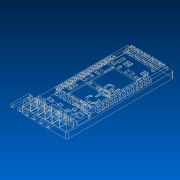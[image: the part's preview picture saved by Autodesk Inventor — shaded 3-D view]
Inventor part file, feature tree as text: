
AUTODESK INVENTOR PART (.ipt)
format: ipt  version: 2015 (Build 190159000, 159)  size: 1,295,360 bytes
history: native  units: mm
features: extrude x16, sketch x13, projected_geometry x8, fillet x5, pattern_linear x3, mirror x1, other x1
ambient origin geometry x8: Origin, YZ Plane, XZ Plane, XY Plane, X Axis, Y Axis, Z Axis, Center Point
bodies: Solid1 (feature_tree)
feature tree (47):
  extrude  "Extrusion1"  Depth=37.5mm
  sketch  "Sketch2"  dims[d2=2.0mm d3=0.0mm d9=0.0mm]
  sketch  "Sketch3"  dims[d12=1.0mm d13=0.0mm d14=1.2mm d15=0.0mm]
  extrude  "Extrusion2"  TaperAngle=0.0deg  [1 undecoded]
  extrude  "Extrusion3"  Depth=1.2mm TaperAngle=0.0deg
  extrude  "Extrusion4"  Depth=1.5mm TaperAngle=0.0deg
  extrude  "Extrusion5"  Depth=1.2mm TaperAngle=0.0deg
  extrude  "Extrusion6"  Depth=130.0mm
  extrude  "Extrusion7"  Depth=1.2mm TaperAngle=0.0deg
  fillet  "Fillet2"  Radius=0.5mm
  pattern_linear  "Rectangular Pattern1"  Count1=8 Spacing1=1.52mm
  mirror  "Mirror1"
  extrude  "Extrusion8"  Depth=0.8mm
  extrude  "Extrusion9"  Depth=4.0mm
  fillet  "Fillet4"  Radius=4.0mm
  pattern_linear  "Rectangular Pattern2"  Count1=6 Spacing1=2.51mm
  extrude  "Extrusion10"  Depth=0.8mm
  pattern_linear  "Rectangular Pattern3"  Spacing1=0.8mm  [1 undecoded]
  extrude  "Extrusion11"  Depth=0.2mm
  extrude  "Extrusion12"  Depth=0.2mm
  fillet  "Fillet5"  Radius=0.8mm
  fillet  "Fillet6"  Radius=0.8mm
  extrude  "Extrusion13"  Depth=2.0mm TaperAngle=0.0deg
  fillet  "Fillet7"  Radius=1.0mm
  extrude  "Extrusion14"  Depth=0.4mm
  extrude  "Extrusion15"  Depth=1.1mm TaperAngle=0.0deg
  extrude  "Extrusion16"  Depth=0.4mm
  sketch  "Sketch1"  dims[d0=16.1mm d1=37.5mm]
  other  "Image2"
  sketch  "Sketch4"  dims[d16=1.5mm d17=0.0mm d18=1.5mm d19=0.0mm]
  sketch  "Sketch5"  dims[d20=1.2mm d21=0.0mm d22=1.2mm d23=0.0mm]
  sketch  "Sketch7"  dims[d26=1.0mm d28=130.0mm]
  sketch  "Sketch8"  dims[d30=18.0mm d31=1.2mm d32=0.0mm d33=0.5mm d34=0.0mm]
  projected_geometry  "Projected Loop2"
  sketch  "Sketch9"  dims[d35=1.0mm d36=80.0mm d38=1.52mm]
  sketch  "Sketch10"  dims[d39=0.8mm d40=0.8mm]
  projected_geometry  "Projected Loop3"
  projected_geometry  "Projected Loop4"
  projected_geometry  "Projected Loop5"
  projected_geometry  "Projected Loop6"
  projected_geometry  "Projected Loop7"
  projected_geometry  "Projected Loop8"
  sketch  "Sketch11"  dims[d41=1.775222mm d42=1.477569mm d43=4.0mm d44=0.0mm d45=60.0mm d47=2.51mm]
  projected_geometry  "Projected Loop9"
  sketch  "Sketch12"  dims[d48=6.7mm d49=0.8mm]
  sketch  "Sketch13"  dims[d50=0.8mm d51=0.0mm]
  sketch  "Sketch14"  dims[d52=0.8mm d53=0.8mm d54=0.8mm d55=0.8mm d56=0.8mm d57=0.8mm d58=2.0mm d59=0.0mm d60=1.0mm d61=0.4mm d62=1.1mm d63=0.0mm d64=0.4mm d65=0.1mm d66=0.0mm d67=0.2mm d68=0.0mm d69=0.2mm d70=0.0mm]
note: 2 required parameter values undecoded (feature->parameter linkage not recoverable at this tier; creation-order binding heuristic only, values carry confidence <= 0.55)
